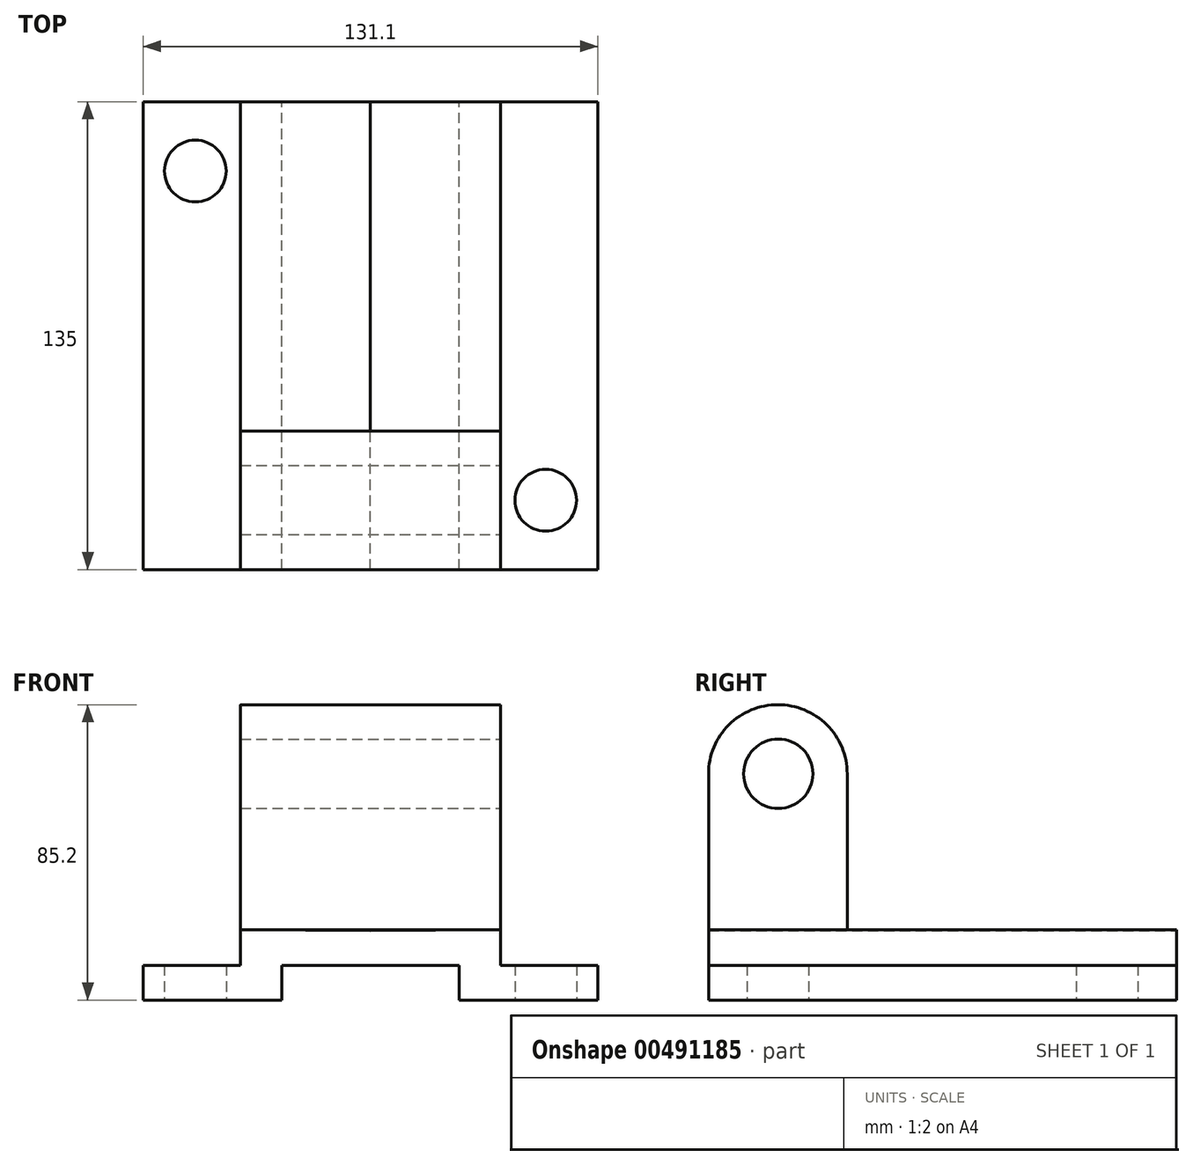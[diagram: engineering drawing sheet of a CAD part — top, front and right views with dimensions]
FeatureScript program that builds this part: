
annotation { "Feature Type Name" : "Feature", "Feature Type Description" : "" }
export const myFeature = defineFeature(function(context is Context, id is Id, definition is map)
    precondition{}
    {
        {
            var Q0;
            Q0=qCreatedBy(makeId("Front.planeOp"),FACE);
            var sketch = newSketch(context, id + "F0", { "sketchPlane" : qUnion([Q0])});
            skLineSegment(sketch, "E0", {"start": v(0, 20) * mm, "end": v(0, 10) * mm});
            skLineSegment(sketch, "E1", {"start": v(0, 10) * mm, "end": v(25.55, 10) * mm});
            skLineSegment(sketch, "E2", {"start": v(25.55, 10) * mm, "end": v(25.55, 0) * mm});
            skLineSegment(sketch, "E3", {"start": v(25.55, 0) * mm, "end": v(65.55, 0) * mm});
            skLineSegment(sketch, "E4", {"start": v(65.55, 0) * mm, "end": v(65.55, 10) * mm});
            skLineSegment(sketch, "E5", {"start": v(65.55, 10) * mm, "end": v(37.5, 10) * mm});
            skLineSegment(sketch, "E6", {"start": v(37.5, 10) * mm, "end": v(37.5, 20.3) * mm});
            skLineSegment(sketch, "E7", {"start": v(37.5, 20.3) * mm, "end": v(0, 20) * mm});
            skLineSegment(sketch, "E8.MirrorCS", {"start": v(-37.5, 20.3) * mm, "end": v(0, 20) * mm});
            skLineSegment(sketch, "E9.MirrorCS", {"start": v(-37.5, 10) * mm, "end": v(-37.5, 20.3) * mm});
            skLineSegment(sketch, "E10.MirrorCS", {"start": v(0, 10) * mm, "end": v(-25.55, 10) * mm});
            skLineSegment(sketch, "E11.MirrorCS", {"start": v(-25.55, 10) * mm, "end": v(-25.55, 0) * mm});
            skLineSegment(sketch, "E12.MirrorCS", {"start": v(-25.55, 0) * mm, "end": v(-65.55, 0) * mm});
            skLineSegment(sketch, "E13.MirrorCS", {"start": v(-65.55, 0) * mm, "end": v(-65.55, 10) * mm});
            skLineSegment(sketch, "E14.MirrorCS", {"start": v(-65.55, 10) * mm, "end": v(-37.5, 10) * mm});
            skSolve(sketch);
        }
        {
            var Q0;
            Q0=makeQuery(id+"F0.imprint","IMPRINT",FACE,{"disambiguationData":[TD([[makeQuery(id+"F0.imprint","IMPRINT",EDGE,{"derivedFrom":sQuery(id+"F0.wireOp",EDGE,"E0")}),-1.0]])]});
            var Q1;
            Q1=makeQuery(id+"F0.imprint","IMPRINT",FACE,{"disambiguationData":[TD([[makeQuery(id+"F0.imprint","IMPRINT",EDGE,{"derivedFrom":sQuery(id+"F0.wireOp",EDGE,"E0")}),1.0]])]});
            extrude(context, id + "F1", {"entities" : qUnion([Q0, Q1]), "endBound" : BoundingType.SYMMETRIC, "depth" : 135 * mm});
        }
        {
            var Q0;
            Q0=qCreatedBy(makeId("Top.planeOp"),FACE);
            var sketch = newSketch(context, id + "F2", { "sketchPlane" : qUnion([Q0])});
            skCircle(sketch, "E15", {"center": v(-50.55, 47.5) * mm, "radius": 8.9 * mm});
            skCircle(sketch, "E16.MirrorC", {"center": v(50.55, 47.5) * mm, "radius": 8.9 * mm});
            skCircle(sketch, "E17.MirrorC", {"center": v(-50.55, -47.5) * mm, "radius": 8.9 * mm});
            skCircle(sketch, "E18.MirrorC", {"center": v(50.55, -47.5) * mm, "radius": 8.9 * mm});
            skPoint(sketch, "E19.0", {"position": v(37.5, -67.5) * mm});
            skLineSegment(sketch, "E19.1", {"start": v(37.5, -67.5) * mm, "end": v(37.5, 67.5) * mm});
            skPoint(sketch, "E19.2", {"position": v(37.5, 0) * mm});
            skSolve(sketch);
        }
        {
            var Q0;
            Q0=makeQuery(id+"F1.opExtrude","SWEPT_FACE",FACE,{"disambiguationData":[OSD([sQuery(id+"F0.wireOp",EDGE,"E6")])]});
            var sketch = newSketch(context, id + "F3", { "sketchPlane" : qUnion([Q0])});
            skPoint(sketch, "E20.0", {"position": v(-67.5, 20.3) * mm});
            skLineSegment(sketch, "E20.1", {"start": v(-67.5, 20.3) * mm, "end": v(67.5, 20.3) * mm});
            skPoint(sketch, "E20.2", {"position": v(0, 20.3) * mm});
            skLineSegment(sketch, "E21", {"start": v(-67.5, 20.3) * mm, "end": v(-67.5, 65.3) * mm});
            skArc(sketch, "E22", {"start": v(-47.5, 85.2) * mm, "mid": v(-61.64, 79.4) * mm, "end": v(-67.5, 65.3) * mm});
            skLineSegment(sketch, "E23", {"start": v(-47.5, 85.2) * mm, "end": v(-47.5, 20.3) * mm, "construction": true});
            skArc(sketch, "E24.MirrorCS", {"start": v(-47.5, 85.2) * mm, "mid": v(-33.36, 79.4) * mm, "end": v(-27.5, 65.3) * mm});
            skLineSegment(sketch, "E25.MirrorCS", {"start": v(-27.5, 20.3) * mm, "end": v(-27.5, 65.3) * mm});
            skCircle(sketch, "E26", {"center": v(-47.4, 65.3) * mm, "radius": 10 * mm});
            skSolve(sketch);
        }
        {
            var Q0;
            Q0 = qSketchRegion(id + "F3", true);
            var Q1;
            Q1=makeQuery(id+"F1.opExtrude","SWEPT_FACE",FACE,{"disambiguationData":[OSD([sQuery(id+"F0.wireOp",EDGE,"E9.MirrorCS")])]});
            extrude(context, id + "F4", {"entities" : qUnion([Q0]), "operationType" : NewBodyOperationType.ADD, "endBound" : BoundingType.UP_TO_SURFACE, "oppositeDirection" : true, "endBoundEntityFace" : qUnion([Q1]), "depth" : 75 * mm});
        }
        {
            var Q0;
            Q0=makeQuery(id+"F2.imprint","IMPRINT",FACE,{"disambiguationData":[TD([[makeQuery(id+"F2.imprint","IMPRINT",EDGE,{"derivedFrom":sQuery(id+"F2.wireOp",EDGE,"E15")}),1.0]])]});
            var Q1;
            Q1=makeQuery(id+"F2.imprint","IMPRINT",FACE,{"disambiguationData":[TD([[makeQuery(id+"F2.imprint","IMPRINT",EDGE,{"derivedFrom":sQuery(id+"F2.wireOp",EDGE,"E17.MirrorC")}),-1.0]])]});
            var Q2;
            Q2=makeQuery(id+"F2.imprint","IMPRINT",FACE,{"disambiguationData":[TD([[makeQuery(id+"F2.imprint","IMPRINT",EDGE,{"derivedFrom":sQuery(id+"F2.wireOp",EDGE,"E18.MirrorC")}),1.0]])]});
            var Q3;
            Q3=makeQuery(id+"F2.imprint","IMPRINT",FACE,{"disambiguationData":[TD([[makeQuery(id+"F2.imprint","IMPRINT",EDGE,{"derivedFrom":sQuery(id+"F2.wireOp",EDGE,"E16.MirrorC")}),-1.0]])]});
            var Q4;
            Q4=sQuery(id+"F2.wireOp",EDGE,"E15");
            var Q5;
            Q5=sQuery(id+"F2.wireOp",EDGE,"E16.MirrorC");
            var Q6;
            Q6=sQuery(id+"F2.wireOp",EDGE,"E17.MirrorC");
            var Q7;
            Q7=sQuery(id+"F2.wireOp",EDGE,"E18.MirrorC");
            extrude(context, id + "F5", {"entities" : qUnion([Q0, Q1, Q2, Q3]), "operationType" : NewBodyOperationType.REMOVE, "surfaceEntities" : qUnion([Q4, Q5, Q6, Q7]), "depth" : 10 * mm});
        }
    });
